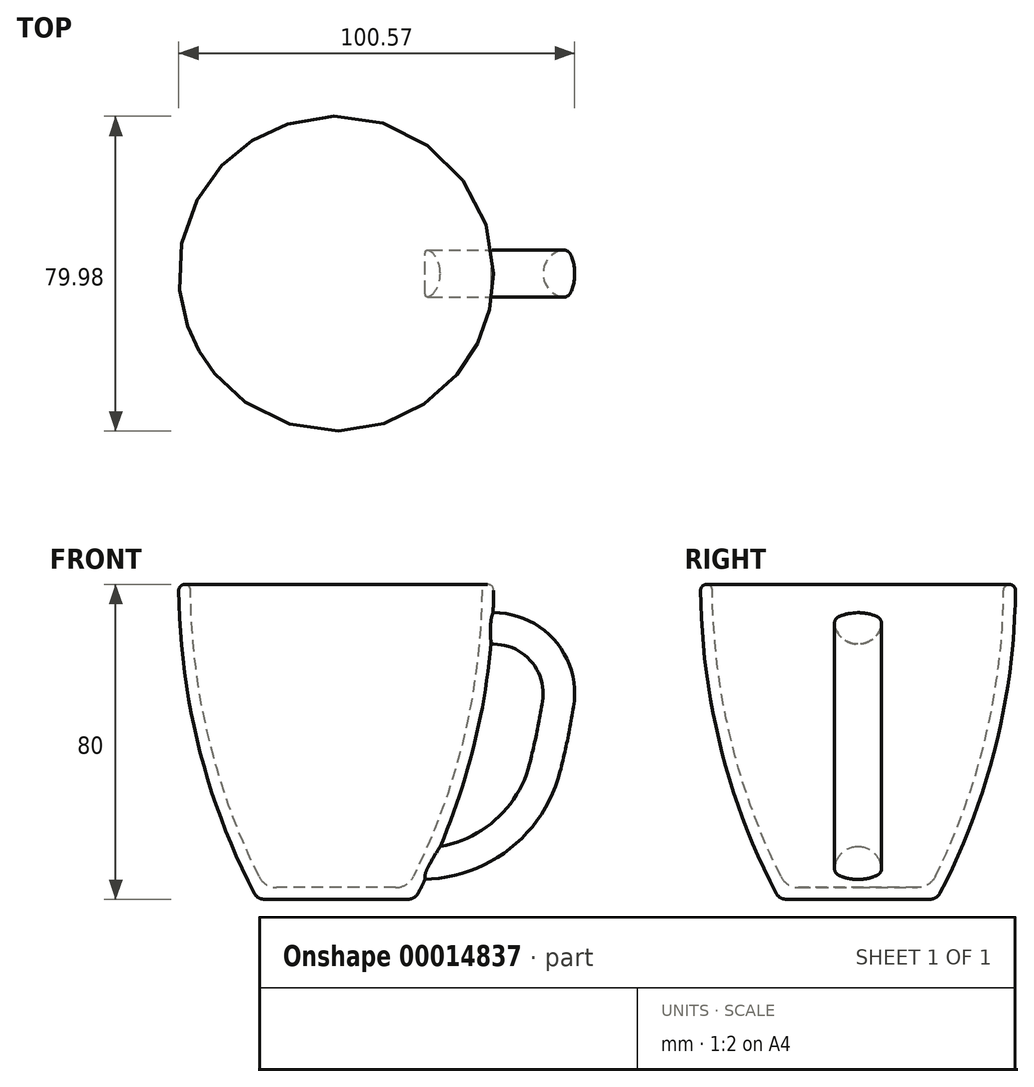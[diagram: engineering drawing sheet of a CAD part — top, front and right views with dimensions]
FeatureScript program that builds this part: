
annotation { "Feature Type Name" : "Feature", "Feature Type Description" : "" }
export const myFeature = defineFeature(function(context is Context, id is Id, definition is map)
    precondition{}
    {
        {
            var Q0;
            Q0=qCreatedBy(makeId("Front.planeOp"),FACE);
            var sketch = newSketch(context, id + "F0", { "sketchPlane" : qUnion([Q0])});
            skLineSegment(sketch, "E0", {"start": v(0, 3) * mm, "end": v(0, 0) * mm});
            skLineSegment(sketch, "E1", {"start": v(0, 0) * mm, "end": v(20, 0) * mm});
            skArc(sketch, "E2", {"start": v(20, 0) * mm, "mid": v(34.92, 38.77) * mm, "end": v(40, 80) * mm});
            skArc(sketch, "E3.0", {"start": v(18.19, 3) * mm, "mid": v(32.23, 40.37) * mm, "end": v(37, 80) * mm});
            skLineSegment(sketch, "E3.1", {"start": v(0, 3) * mm, "end": v(18.19, 3) * mm});
            skLineSegment(sketch, "E4", {"start": v(37, 80) * mm, "end": v(40, 80) * mm});
            skLineSegment(sketch, "E5", {"start": v(40, 160) * mm, "end": v(40, 0) * mm, "construction": true});
            skLineSegment(sketch, "E6", {"start": v(37, 160) * mm, "end": v(37, 0) * mm, "construction": true});
            skSolve(sketch);
        }
        {
            var Q0;
            Q0 = qSketchRegion(id + "F0", true);
            var Q1;
            Q1=sQuery(id+"F0.wireOp",EDGE,"E0");
            revolve(context, id + "F1", {"entities" : qUnion([Q0]), "axis" : qUnion([Q1]), "revolveType" : RevolveType.FULL});
        }
        {
            var Q0;
            Q0=sQuery(id+"F0.wireOp",EDGE,"E5");
            cPlane(context, id + "F2", {"entities" : qUnion([Q0]), "cplaneType" : CPlaneType.LINE_ANGLE, "offset" : 150 * mm, "angle" : 0 * degree, "width" : 150 * mm, "height" : 150 * mm});
        }
        {
            var Q0;
            Q0=qCreatedBy(id+"F2.planeOp",FACE);
            var sketch = newSketch(context, id + "F3", { "sketchPlane" : qUnion([Q0])});
            skPoint(sketch, "E7", {"position": v(0, 70) * mm});
            skArc(sketch, "E8", {"start": v(4.8, 71.83) * mm, "mid": v(0, 72.83) * mm, "end": v(-4.8, 71.83) * mm});
            skArc(sketch, "E9", {"start": v(4.8, 71.83) * mm, "mid": v(5.79, 70.9) * mm, "end": v(5.95, 69.54) * mm});
            skArc(sketch, "E10", {"start": v(-4.8, 71.83) * mm, "mid": v(-5.79, 70.9) * mm, "end": v(-5.95, 69.54) * mm});
            skArc(sketch, "E11", {"start": v(-5.95, 69.54) * mm, "mid": v(0, 64.83) * mm, "end": v(5.95, 69.54) * mm});
            skSolve(sketch);
        }
        {
            var Q0;
            Q0 = qSketchRegion(id + "F3", true);
            extrude(context, id + "F4", {"entities" : qUnion([Q0]), "operationType" : NewBodyOperationType.ADD, "endBound" : BoundingType.UP_TO_NEXT, "depth" : 25 * mm});
        }
        {
            var Q0;
            Q0=qCreatedBy(makeId("Front.planeOp"),FACE);
            var sketch = newSketch(context, id + "F5", { "sketchPlane" : qUnion([Q0])});
            skArc(sketch, "E12", {"start": v(57.52, 49.4) * mm, "mid": v(53.52, 63.75) * mm, "end": v(40, 70) * mm});
            skLineSegment(sketch, "E13", {"start": v(42.52, 70) * mm, "end": v(37.48, 70) * mm, "construction": true});
            skArc(sketch, "E14", {"start": v(54.14, 33.16) * mm, "mid": v(56, 41.24) * mm, "end": v(57.52, 49.4) * mm});
            skArc(sketch, "E15", {"start": v(54.14, 33.16) * mm, "mid": v(43.14, 15.7) * mm, "end": v(24, 8) * mm});
            skLineSegment(sketch, "E16", {"start": v(-130, 80) * mm, "end": v(57.52, 49.4) * mm, "construction": true});
            skLineSegment(sketch, "E17", {"start": v(-130, 80) * mm, "end": v(54.14, 33.16) * mm, "construction": true});
            skSolve(sketch);
        }
        {
            var Q0;
            Q0=makeQuery(id+"F3.imprint","IMPRINT",FACE,{"disambiguationData":[TD([[makeQuery(id+"F3.imprint","IMPRINT",EDGE,{"derivedFrom":sQuery(id+"F3.wireOp",EDGE,"E8")}),1.0]])]});
            var Q1;
            Q1=sQuery(id+"F5.wireOp",EDGE,"E12");
            var Q2;
            Q2=sQuery(id+"F5.wireOp",EDGE,"E14");
            var Q3;
            Q3=sQuery(id+"F5.wireOp",EDGE,"E15");
            sweep(context, id + "F6", {"operationType" : NewBodyOperationType.ADD, "profiles" : qUnion([Q0]), "path" : qUnion([Q1, Q2, Q3])});
        }
        {
            var Q0;
            Q0=makeQuery(id+"F1.opRevolve","SWEPT_EDGE",EDGE,{"disambiguationData":[OSD([sQuery(id+"F0.wireOp",EDGE,"E3.0"),sQuery(id+"F0.wireOp",EDGE,"E4")])]});
            var Q1;
            Q1=makeQuery(id+"F1.opRevolve","SWEPT_EDGE",EDGE,{"disambiguationData":[OSD([sQuery(id+"F0.wireOp",EDGE,"E2"),sQuery(id+"F0.wireOp",EDGE,"E4")])]});
            fillet(context, id + "F7", {"entities" : qUnion([Q0, Q1]), "radius" : 1.5 * mm, "tangentPropagation" : true, "allowEdgeOverflow" : false});
        }
        {
            var Q0;
            Q0=makeQuery(id+"F1.opRevolve","SWEPT_EDGE",EDGE,{"disambiguationData":[OSD([sQuery(id+"F0.wireOp",EDGE,"E1"),sQuery(id+"F0.wireOp",EDGE,"E2")])]});
            fillet(context, id + "F8", {"entities" : qUnion([Q0]), "radius" : 3 * mm, "tangentPropagation" : true, "allowEdgeOverflow" : false});
        }
        {
            var Q0;
            Q0=makeQuery(id+"F1.opRevolve","SWEPT_EDGE",EDGE,{"disambiguationData":[OSD([sQuery(id+"F0.wireOp",EDGE,"E3.0"),sQuery(id+"F0.wireOp",EDGE,"E3.1")])]});
            fillet(context, id + "F9", {"entities" : qUnion([Q0]), "radius" : 5 * mm, "tangentPropagation" : true, "allowEdgeOverflow" : false});
        }
        {
            var Q0;
            Q0=makeQuery(id+"F6.opSweep","CAP_FACE",FACE,{"disambiguationData":[OSD([sQuery(id+"F3.wireOp",EDGE,"E8"),sQuery(id+"F3.wireOp",EDGE,"E9"),sQuery(id+"F3.wireOp",EDGE,"E10"),sQuery(id+"F3.wireOp",EDGE,"E11"),sQuery(id+"F5.wireOp",VERTEX,"E15.end")])],"isStart":false});
            var sketch = newSketch(context, id + "F10", { "sketchPlane" : qUnion([Q0])});
            skArc(sketch, "E18", {"start": v(5.95, 6.77) * mm, "mid": v(5.84, 7.17) * mm, "end": v(5.7, 7.57) * mm});
            skArc(sketch, "E19", {"start": v(4.8, 4.48) * mm, "mid": v(5.79, 5.41) * mm, "end": v(5.95, 6.77) * mm});
            skArc(sketch, "E20", {"start": v(-4.8, 4.48) * mm, "mid": v(0, 3.47) * mm, "end": v(4.8, 4.48) * mm});
            skArc(sketch, "E21", {"start": v(-5.95, 6.77) * mm, "mid": v(-5.79, 5.41) * mm, "end": v(-4.8, 4.48) * mm});
            skArc(sketch, "E22", {"start": v(-5.7, 7.57) * mm, "mid": v(-5.84, 7.17) * mm, "end": v(-5.95, 6.77) * mm});
            skLineSegment(sketch, "E23", {"start": v(5.7, 7.57) * mm, "end": v(-5.7, 7.57) * mm});
            skSolve(sketch);
        }
        {
            var Q0;
            Q0 = qSketchRegion(id + "F10", true);
            var Q1;
            Q1=makeQuery(id+"F1.opRevolve","SWEPT_FACE",FACE,{"disambiguationData":[OSD([sQuery(id+"F0.wireOp",EDGE,"E3.0")])]});
            extrude(context, id + "F11", {"entities" : qUnion([Q0]), "operationType" : NewBodyOperationType.ADD, "endBound" : BoundingType.UP_TO_SURFACE, "endBoundEntityFace" : qUnion([Q1]), "depth" : 25 * mm});
        }
    });
